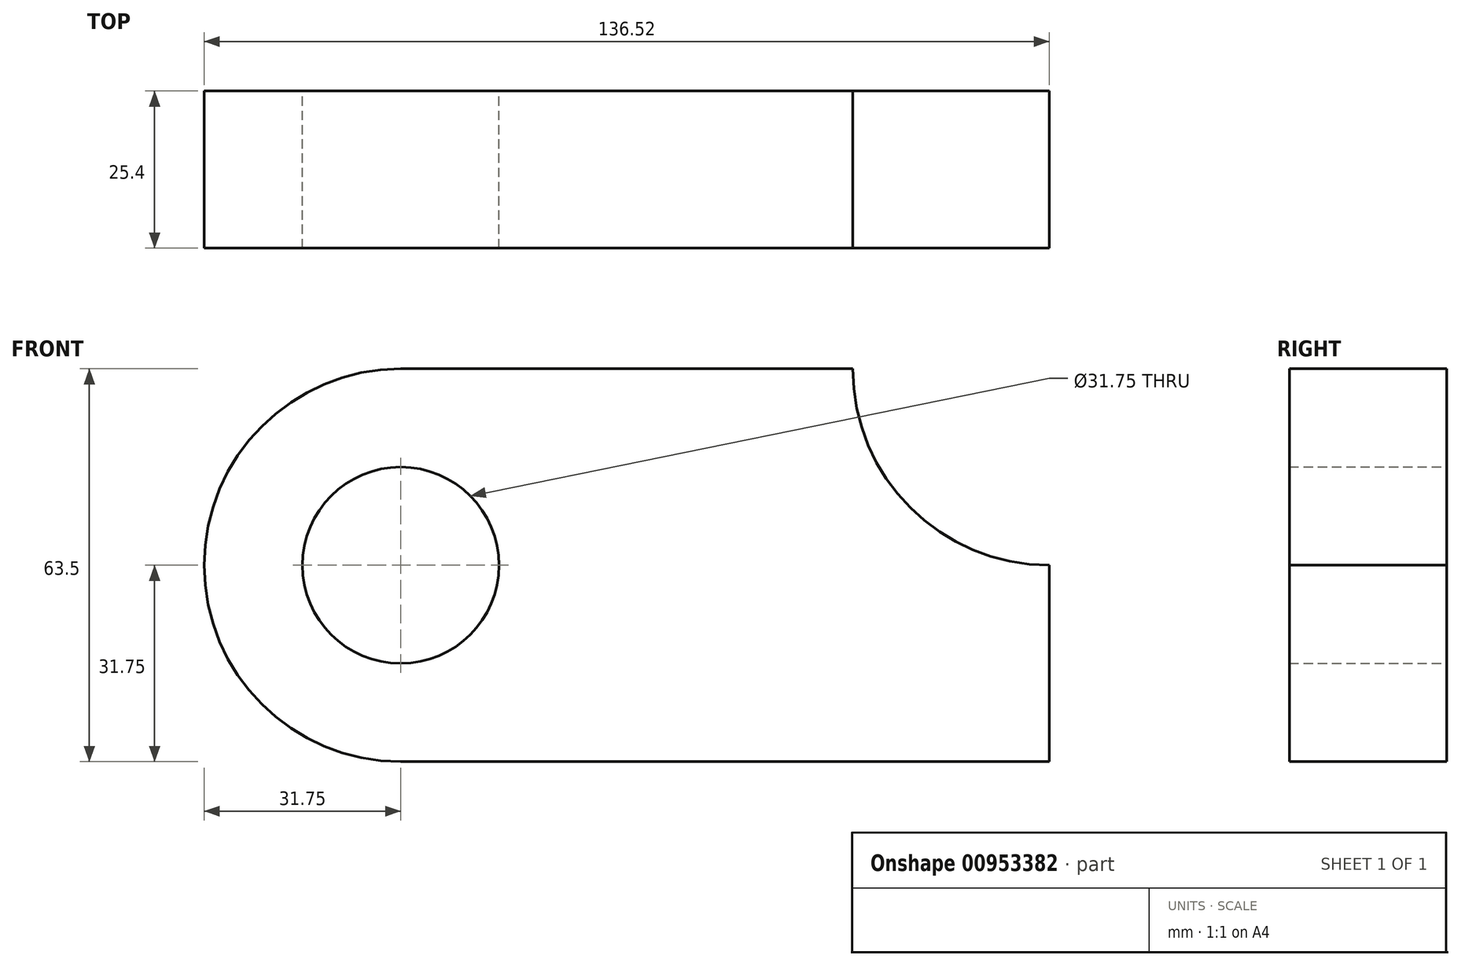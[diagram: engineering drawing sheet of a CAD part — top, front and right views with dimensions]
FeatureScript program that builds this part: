
annotation { "Feature Type Name" : "Feature", "Feature Type Description" : "" }
export const myFeature = defineFeature(function(context is Context, id is Id, definition is map)
    precondition{}
    {
        {
            var Q0;
            Q0=qCreatedBy(makeId("Front.planeOp"),FACE);
            var sketch = newSketch(context, id + "F0", { "sketchPlane" : qUnion([Q0])});
            skLineSegment(sketch, "E0", {"start": v(0, 0) * mm, "end": v(104.77, 0) * mm});
            skLineSegment(sketch, "E1", {"start": v(0, 0) * mm, "end": v(0, 31.75) * mm});
            skCircle(sketch, "E2", {"center": v(0, 31.75) * mm, "radius": 15.88 * mm});
            skLineSegment(sketch, "E3", {"start": v(0, 31.75) * mm, "end": v(0, 63.5) * mm});
            skLineSegment(sketch, "E4", {"start": v(0, 63.5) * mm, "end": v(73.03, 63.5) * mm});
            skLineSegment(sketch, "E5", {"start": v(104.77, 0) * mm, "end": v(104.77, 31.75) * mm});
            skArc(sketch, "E6", {"start": v(104.77, 31.75) * mm, "mid": v(104.7, 30.73) * mm, "end": v(104.6, 29.72) * mm});
            skArc(sketch, "E7", {"start": v(73.03, 63.5) * mm, "mid": v(82.32, 41.05) * mm, "end": v(104.77, 31.75) * mm});
            skArc(sketch, "E8", {"start": v(0, 63.5) * mm, "mid": v(-31.75, 31.75) * mm, "end": v(0, 0) * mm});
            skSolve(sketch);
        }
        {
            var Q0;
            {var subQ7=sQuery(id+"F0.wireOp",EDGE,"E0");Q0=makeQuery(id+"F0.imprint","IMPRINT",FACE,{"disambiguationData":[TD([[makeQuery(id+"F0.imprint","IMPRINT",EDGE,{"derivedFrom":subQ7}),1.0]])]});}
            var Q1;
            {var subQ0=sQuery(id+"F0.wireOp",EDGE,"E8");Q1=makeQuery(id+"F0.imprint","IMPRINT",FACE,{"disambiguationData":[TD([[makeQuery(id+"F0.imprint","IMPRINT",EDGE,{"derivedFrom":subQ0}),1.0]])]});}
            extrude(context, id + "F1", {"entities" : qUnion([Q0, Q1]), "depth" : 25.4 * mm, "offsetDistance" : 25.4 * mm});
        }
    });
